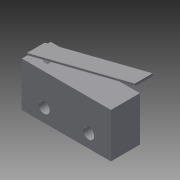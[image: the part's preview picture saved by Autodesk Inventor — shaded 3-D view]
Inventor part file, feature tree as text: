
AUTODESK INVENTOR PART (.ipt)
format: ipt  version: 2013 SP2 (Build 170200200, 200)  size: 107,008 bytes
history: native  units: mm
features: extrude x4, sketch x4, plane x1
ambient origin geometry x8: Origin, YZ Plane, XZ Plane, XY Plane, X Axis, Y Axis, Z Axis, Center Point
bodies: Solid1 (feature_tree)
feature tree (9):
  extrude  "Extrusion1"  Depth=6.5mm
  extrude  "Extrusion2"  Depth=1.0mm
  extrude  "Extrusion3"  Depth=3.0mm
  plane  "Work Plane1"
  extrude  "Extrusion4"  Depth=2.5mm
  sketch  "Sketch1"  dims[d0=20.0mm d1=6.5mm]
  sketch  "Sketch2"  dims[d2=10.0mm d3=0.0mm d4=1.0mm]
  sketch  "Sketch3"  dims[d5=3.0mm d6=3.0mm]
  sketch  "Sketch4"  dims[d7=1.0mm d8=0.0mm d9=2.5mm d10=2.5mm d11=3.0mm d12=10.0mm d13=2.0mm d14=0.0mm d15=0.4mm d16=4.0mm d17=0.0mm d19=25.0mm]
